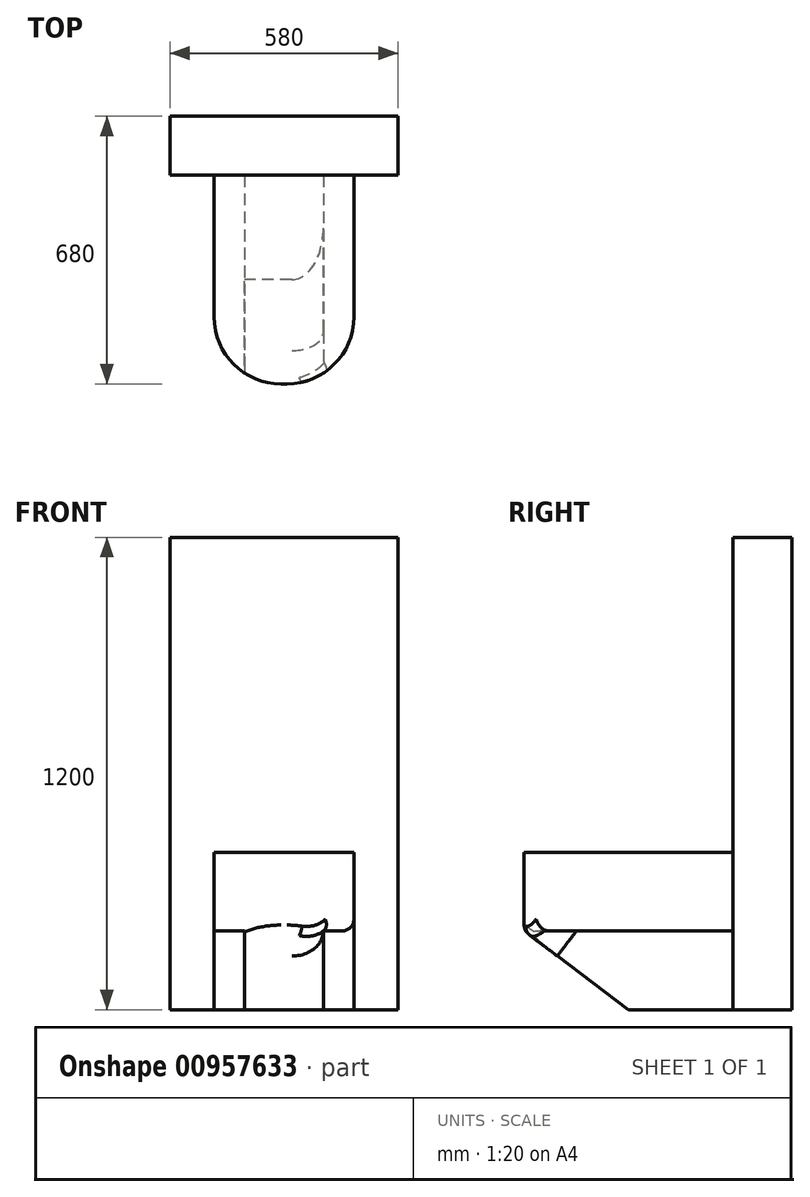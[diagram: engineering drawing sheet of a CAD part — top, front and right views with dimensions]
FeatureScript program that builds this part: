
annotation { "Feature Type Name" : "Feature", "Feature Type Description" : "" }
export const myFeature = defineFeature(function(context is Context, id is Id, definition is map)
    precondition{}
    {
        {
            var Q0;
            Q0=qCreatedBy(makeId("Top.planeOp"),FACE);
            var sketch = newSketch(context, id + "F0", { "sketchPlane" : qUnion([Q0])});
            skLineSegment(sketch, "E0.bottom", {"start": v(177.5, -340) * mm, "end": v(-177.5, -340) * mm});
            skLineSegment(sketch, "E0.top", {"start": v(177.5, 340) * mm, "end": v(-177.5, 340) * mm});
            skLineSegment(sketch, "E0.left", {"start": v(177.5, -340) * mm, "end": v(177.5, 340) * mm});
            skLineSegment(sketch, "E0.right", {"start": v(-177.5, -340) * mm, "end": v(-177.5, 340) * mm});
            skPoint(sketch, "E0.middle", {"position": v(0, 0) * mm});
            skSolve(sketch);
        }
        {
            var Q0;
            Q0=makeQuery(id+"F0.imprint","IMPRINT",FACE,{"disambiguationData":[TD([[makeQuery(id+"F0.imprint","IMPRINT",EDGE,{"derivedFrom":sQuery(id+"F0.wireOp",EDGE,"E0.bottom")}),-1.0]])]});
            extrude(context, id + "F1", {"entities" : qUnion([Q0]), "depth" : 400 * mm, "offsetDistance" : 25 * mm});
        }
        {
            var Q0;
            Q0=makeQuery(id+"F1.opExtrude","SWEPT_FACE",FACE,{"disambiguationData":[OSD([sQuery(id+"F0.wireOp",EDGE,"E0.bottom")])]});
            var sketch = newSketch(context, id + "F2", { "sketchPlane" : qUnion([Q0])});
            skLineSegment(sketch, "E1.bottom", {"start": v(-177.5, 200) * mm, "end": v(-100, 200) * mm});
            skLineSegment(sketch, "E1.top", {"start": v(-177.5, 0) * mm, "end": v(-100, 0) * mm});
            skLineSegment(sketch, "E1.left", {"start": v(-177.5, 200) * mm, "end": v(-177.5, 0) * mm});
            skLineSegment(sketch, "E1.right", {"start": v(-100, 200) * mm, "end": v(-100, 0) * mm});
            skLineSegment(sketch, "E2.MirrorCS", {"start": v(177.5, 200) * mm, "end": v(177.5, 0) * mm});
            skLineSegment(sketch, "E3.MirrorCS", {"start": v(177.5, 200) * mm, "end": v(100, 200) * mm});
            skLineSegment(sketch, "E4.MirrorCS", {"start": v(177.5, 0) * mm, "end": v(100, 0) * mm});
            skLineSegment(sketch, "E5.MirrorCS", {"start": v(100, 200) * mm, "end": v(100, 0) * mm});
            skSolve(sketch);
        }
        {
            var Q0;
            Q0=makeQuery(id+"F2.imprint","IMPRINT",FACE,{"disambiguationData":[TD([[makeQuery(id+"F2.imprint","IMPRINT",EDGE,{"derivedFrom":sQuery(id+"F2.wireOp",EDGE,"E1.bottom")}),-1.0]])]});
            var Q1;
            Q1=makeQuery(id+"F2.imprint","IMPRINT",FACE,{"disambiguationData":[TD([[makeQuery(id+"F2.imprint","IMPRINT",EDGE,{"derivedFrom":sQuery(id+"F2.wireOp",EDGE,"E2.MirrorCS")}),-1.0]])]});
            extrude(context, id + "F3", {"entities" : qUnion([Q0, Q1]), "operationType" : NewBodyOperationType.REMOVE, "oppositeDirection" : true, "depth" : 530 * mm, "offsetDistance" : 25 * mm});
        }
        {
            var Q0;
            Q0=makeQuery(id+"F3.boolean.opBoolean","COPY",FACE,{"derivedFrom":makeQuery(id+"F3.opExtrude","SWEPT_FACE",FACE,{"disambiguationData":[OSD([sQuery(id+"F2.wireOp",EDGE,"E1.right")])]})});
            var sketch = newSketch(context, id + "F4", { "sketchPlane" : qUnion([Q0])});
            skLineSegment(sketch, "E6", {"start": v(340, 200) * mm, "end": v(75, 0) * mm});
            skLineSegment(sketch, "E7", {"start": v(75, 0) * mm, "end": v(340, 0) * mm});
            skLineSegment(sketch, "E8", {"start": v(340, 0) * mm, "end": v(340, 200) * mm});
            skSolve(sketch);
        }
        {
            var Q0;
            Q0=makeQuery(id+"F4.imprint","IMPRINT",FACE,{"disambiguationData":[TD([[makeQuery(id+"F4.imprint","IMPRINT",EDGE,{"derivedFrom":sQuery(id+"F4.wireOp",EDGE,"E6")}),1.0]])]});
            extrude(context, id + "F5", {"entities" : qUnion([Q0]), "operationType" : NewBodyOperationType.REMOVE, "oppositeDirection" : true, "depth" : 600 * mm, "offsetDistance" : 25 * mm});
        }
        {
            var Q0;
            Q0=makeQuery(id+"F1.opExtrude","SWEPT_EDGE",EDGE,{"disambiguationData":[OSD([sQuery(id+"F0.wireOp",EDGE,"E0.bottom"),sQuery(id+"F0.wireOp",EDGE,"E0.right")])]});
            var Q1;
            Q1=makeQuery(id+"F1.opExtrude","SWEPT_EDGE",EDGE,{"disambiguationData":[OSD([sQuery(id+"F0.wireOp",EDGE,"E0.bottom"),sQuery(id+"F0.wireOp",EDGE,"E0.left")])]});
            fillet(context, id + "F6", {"entities" : qUnion([Q0, Q1]), "radius" : 170 * mm, "tangentPropagation" : true, "allowEdgeOverflow" : false});
        }
        {
            var Q0;
            Q0=makeQuery(id+"F5.boolean.opBoolean","COPY",EDGE,{"derivedFrom":makeQuery(id+"F5.opExtrude","CAP_EDGE",EDGE,{"disambiguationData":[OSD([sQuery(id+"F4.wireOp",EDGE,"E6")])],"isStart":true})});
            var Q1;
            Q1=makeQuery(id+"F5.boolean.opBoolean","INTERSECT",EDGE,{"derivedFrom":[makeQuery(id+"F3.boolean.opBoolean","COPY",FACE,{"derivedFrom":makeQuery(id+"F3.opExtrude","SWEPT_FACE",FACE,{"disambiguationData":[OSD([sQuery(id+"F2.wireOp",EDGE,"E5.MirrorCS")])]})}),makeQuery(id+"F5.opExtrude","SWEPT_FACE",FACE,{"disambiguationData":[OSD([sQuery(id+"F4.wireOp",EDGE,"E6")])]})]});
            fillet(context, id + "F7", {"entities" : qUnion([Q0, Q1]), "radius" : 80 * mm, "tangentPropagation" : true, "allowEdgeOverflow" : false});
        }
        {
            var Q0;
            Q0=makeQuery(id+"F3.boolean.opBoolean","COPY",EDGE,{"derivedFrom":makeQuery(id+"F3.opExtrude","SWEPT_EDGE",EDGE,{"disambiguationData":[OSD([sQuery(id+"F0.wireOp",EDGE,"E0.bottom"),sQuery(id+"F0.wireOp",EDGE,"E0.left"),sQuery(id+"F2.wireOp",EDGE,"E2.MirrorCS"),sQuery(id+"F2.wireOp",EDGE,"E3.MirrorCS")])]})});
            var Q1;
            Q1=makeQuery(id+"F3.boolean.opBoolean","COPY",EDGE,{"derivedFrom":makeQuery(id+"F3.opExtrude","SWEPT_EDGE",EDGE,{"disambiguationData":[OSD([sQuery(id+"F0.wireOp",EDGE,"E0.bottom"),sQuery(id+"F0.wireOp",EDGE,"E0.right"),sQuery(id+"F2.wireOp",EDGE,"E1.bottom"),sQuery(id+"F2.wireOp",EDGE,"E1.left")])]})});
            var Q2;
            Q2=makeQuery(id+"F7.opFillet","BLEND_EDGE",EDGE,{"blendedFrom":[makeQuery(id+"F5.boolean.opBoolean","INTERSECT",EDGE,{"derivedFrom":[makeQuery(id+"F3.boolean.opBoolean","COPY",FACE,{"derivedFrom":makeQuery(id+"F3.opExtrude","SWEPT_FACE",FACE,{"disambiguationData":[OSD([sQuery(id+"F2.wireOp",EDGE,"E5.MirrorCS")])]})}),makeQuery(id+"F5.opExtrude","SWEPT_FACE",FACE,{"disambiguationData":[OSD([sQuery(id+"F4.wireOp",EDGE,"E6")])]})]}),makeQuery(id+"F6.opFillet","BLEND_FACE",FACE,{"disambiguationData":[OSD([sQuery(id+"F0.wireOp",EDGE,"E0.bottom"),sQuery(id+"F0.wireOp",EDGE,"E0.left")])]})],"blendedInto":[makeQuery(id+"F6.opFillet","BLEND_FACE",FACE,{"disambiguationData":[OSD([sQuery(id+"F0.wireOp",EDGE,"E0.bottom"),sQuery(id+"F0.wireOp",EDGE,"E0.left")])]})]});
            fillet(context, id + "F8", {"entities" : qUnion([Q0, Q1, Q2]), "radius" : 30 * mm, "tangentPropagation" : true, "allowEdgeOverflow" : false});
        }
        {
            var Q0;
            Q0=makeQuery(id+"F1.opExtrude","CAP_FACE",FACE,{"disambiguationData":[OSD([sQuery(id+"F0.wireOp",EDGE,"E0.bottom"),sQuery(id+"F0.wireOp",EDGE,"E0.top"),sQuery(id+"F0.wireOp",EDGE,"E0.left"),sQuery(id+"F0.wireOp",EDGE,"E0.right")])],"isStart":true});
            var sketch = newSketch(context, id + "F9", { "sketchPlane" : qUnion([Q0])});
            skLineSegment(sketch, "E9.bottom", {"start": v(290, -190.6) * mm, "end": v(-290, -190.6) * mm});
            skLineSegment(sketch, "E9.top", {"start": v(290, -340) * mm, "end": v(-290, -340) * mm});
            skLineSegment(sketch, "E9.left", {"start": v(290, -190.6) * mm, "end": v(290, -340) * mm});
            skLineSegment(sketch, "E9.right", {"start": v(-290, -190.6) * mm, "end": v(-290, -340) * mm});
            skPoint(sketch, "E9.middle", {"position": v(0, -265.3) * mm});
            skPoint(sketch, "E9.cornerSnap0", {"position": v(20, -190.6) * mm});
            skSolve(sketch);
        }
        {
            var Q0;
            Q0 = qSketchRegion(id + "F9", true);
            extrude(context, id + "F10", {"entities" : qUnion([Q0]), "operationType" : NewBodyOperationType.ADD, "flatOperationType" : FlatOperationType.REMOVE, "oppositeDirection" : true, "depth" : 1200 * mm, "offsetDistance" : 25 * mm, "domain" : OperationDomain.MODEL});
        }
    });
